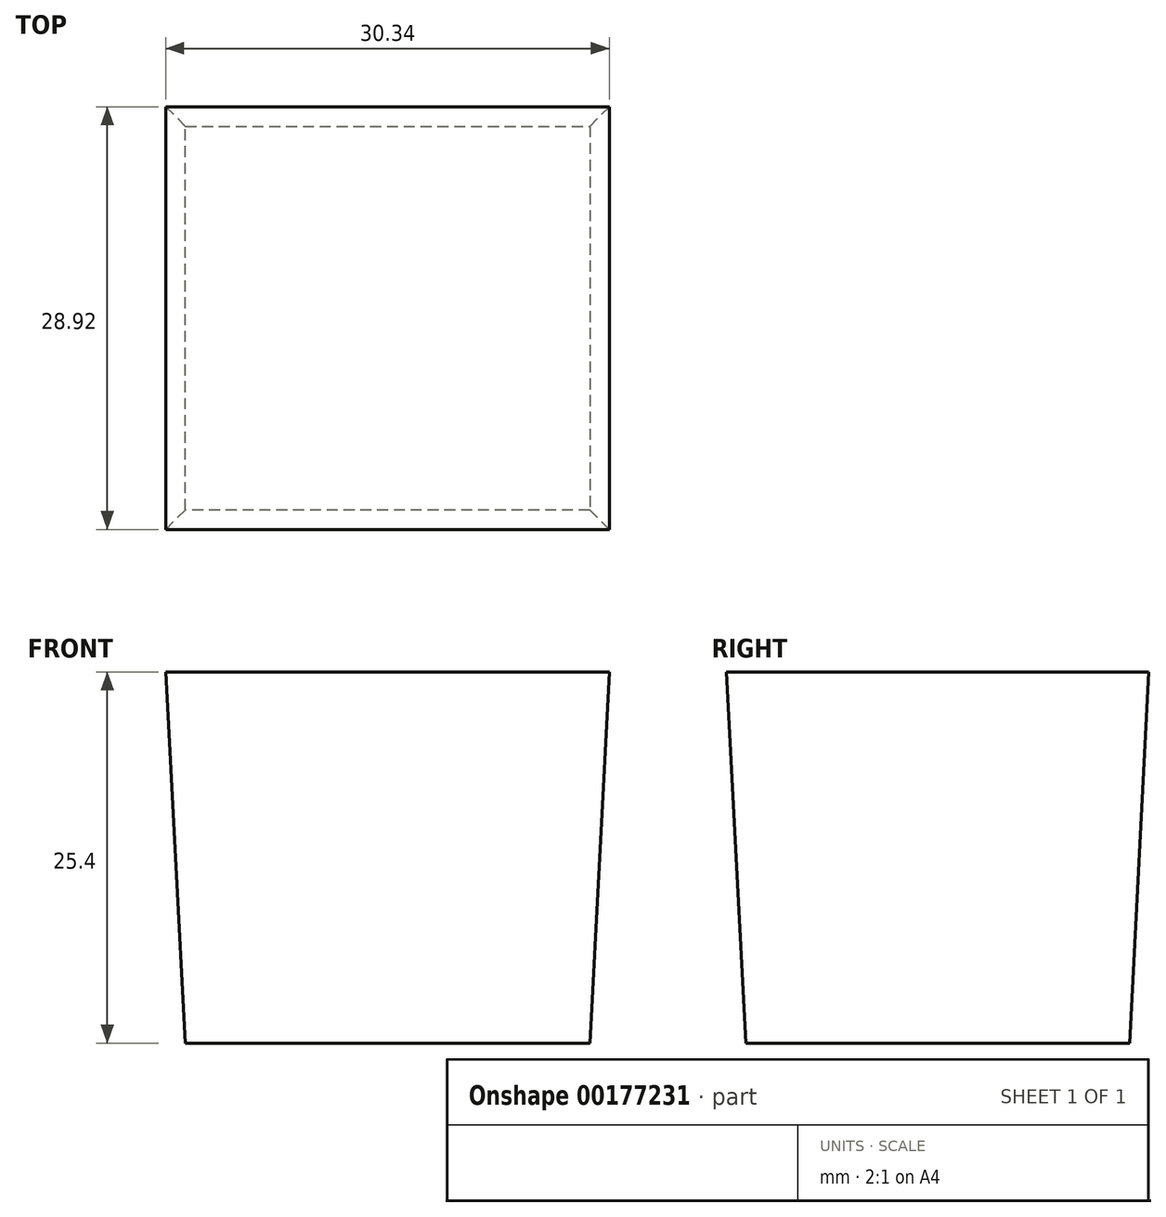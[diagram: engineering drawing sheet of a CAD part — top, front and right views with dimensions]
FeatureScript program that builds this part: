
annotation { "Feature Type Name" : "Feature", "Feature Type Description" : "" }
export const myFeature = defineFeature(function(context is Context, id is Id, definition is map)
    precondition{}
    {
        {
            var Q0;
            Q0=qCreatedBy(makeId("Top.planeOp"),FACE);
            var sketch = newSketch(context, id + "F0", { "sketchPlane" : qUnion([Q0])});
            skLineSegment(sketch, "E0.bottom", {"start": v(13.84, 13.13) * mm, "end": v(-13.84, 13.13) * mm});
            skLineSegment(sketch, "E0.top", {"start": v(13.84, -13.13) * mm, "end": v(-13.84, -13.13) * mm});
            skLineSegment(sketch, "E0.left", {"start": v(13.84, 13.13) * mm, "end": v(13.84, -13.13) * mm});
            skLineSegment(sketch, "E0.right", {"start": v(-13.84, 13.13) * mm, "end": v(-13.84, -13.13) * mm});
            skPoint(sketch, "E0.middle", {"position": v(0, 0) * mm});
            skSolve(sketch);
        }
        {
            var Q0;
            Q0=makeQuery(id+"F0.imprint","IMPRINT",FACE,{"disambiguationData":[TD([[makeQuery(id+"F0.imprint","IMPRINT",EDGE,{"derivedFrom":sQuery(id+"F0.wireOp",EDGE,"E0.bottom")}),1.0]])]});
            extrude(context, id + "F1", {"entities" : qUnion([Q0]), "depth" : 25.4 * mm, "hasDraft" : true, "draftAngle" : 3 * degree});
        }
    });
